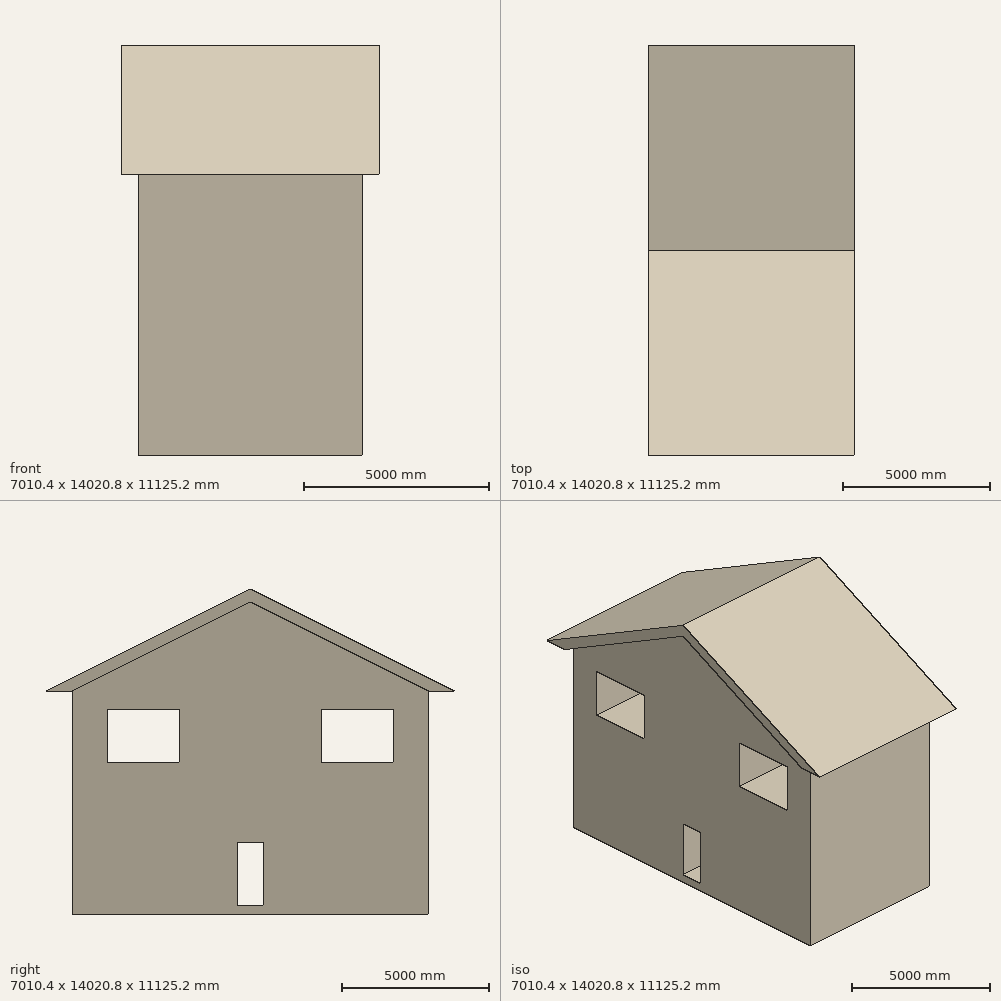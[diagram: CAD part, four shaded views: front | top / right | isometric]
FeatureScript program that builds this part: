
annotation { "Feature Type Name" : "Feature", "Feature Type Description" : "" }
export const myFeature = defineFeature(function(context is Context, id is Id, definition is map)
    precondition{}
    {
        {
            var Q0;
            Q0=qCreatedBy(makeId("Right.planeOp"),FACE);
            var sketch = newSketch(context, id + "F0", { "sketchPlane" : qUnion([Q0])});
            skLineSegment(sketch, "E0", {"start": v(0, 0) * mm, "end": v(-6096, 0) * mm});
            skLineSegment(sketch, "E1", {"start": v(-6096, 0) * mm, "end": v(-12192, 0) * mm});
            skLineSegment(sketch, "E2", {"start": v(-12192, 0) * mm, "end": v(-6096, 3048) * mm});
            skLineSegment(sketch, "E3", {"start": v(0, 0) * mm, "end": v(-6096, 3048) * mm});
            skLineSegment(sketch, "E4", {"start": v(-12192, 0) * mm, "end": v(-12192, -7315.2) * mm});
            skLineSegment(sketch, "E5", {"start": v(-12192, -7315.2) * mm, "end": v(0, -7315.2) * mm});
            skLineSegment(sketch, "E6", {"start": v(0, 0) * mm, "end": v(0, -7315.2) * mm});
            skLineSegment(sketch, "E7", {"start": v(-12192, -7315.2) * mm, "end": v(-12192, -7620) * mm});
            skLineSegment(sketch, "E8", {"start": v(0, -7315.2) * mm, "end": v(0, -7620) * mm});
            skLineSegment(sketch, "E9", {"start": v(-12192, -7620) * mm, "end": v(0, -7620) * mm});
            skLineSegment(sketch, "E10", {"start": v(-6096, -7315.2) * mm, "end": v(-6553.2, -7315.2) * mm});
            skLineSegment(sketch, "E11", {"start": v(-6553.2, -7315.2) * mm, "end": v(-6553.2, -5181.6) * mm});
            skLineSegment(sketch, "E12", {"start": v(-6553.2, -5181.6) * mm, "end": v(-5638.8, -5181.6) * mm});
            skLineSegment(sketch, "E13", {"start": v(-5638.8, -5181.6) * mm, "end": v(-5638.8, -7315.2) * mm});
            skLineSegment(sketch, "E14", {"start": v(-12192, 0) * mm, "end": v(-13106.4, 0) * mm});
            skLineSegment(sketch, "E15", {"start": v(0, 0) * mm, "end": v(914.4, 0) * mm});
            skLineSegment(sketch, "E16", {"start": v(-6096, 3048) * mm, "end": v(-6096, 3505.2) * mm});
            skLineSegment(sketch, "E17", {"start": v(-6096, 3505.2) * mm, "end": v(-13106.4, 0) * mm});
            skLineSegment(sketch, "E18", {"start": v(-6096, 3505.2) * mm, "end": v(914.4, 0) * mm});
            skLineSegment(sketch, "E19.bottom", {"start": v(-10668, -914.4) * mm, "end": v(-8839.2, -914.4) * mm});
            skLineSegment(sketch, "E19.top", {"start": v(-10668, -2133.6) * mm, "end": v(-8839.2, -2133.6) * mm});
            skLineSegment(sketch, "E19.left", {"start": v(-10668, -914.4) * mm, "end": v(-10668, -2133.6) * mm});
            skLineSegment(sketch, "E19.right", {"start": v(-8839.2, -914.4) * mm, "end": v(-8839.2, -2133.6) * mm});
            skLineSegment(sketch, "E20.bottom", {"start": v(-3352.8, -914.4) * mm, "end": v(-1524, -914.4) * mm});
            skLineSegment(sketch, "E20.top", {"start": v(-3352.8, -2133.6) * mm, "end": v(-1524, -2133.6) * mm});
            skLineSegment(sketch, "E20.left", {"start": v(-3352.8, -914.4) * mm, "end": v(-3352.8, -2133.6) * mm});
            skLineSegment(sketch, "E20.right", {"start": v(-1524, -914.4) * mm, "end": v(-1524, -2133.6) * mm});
            skLineSegment(sketch, "E21.0", {"start": v(-1219.2, -609.6) * mm, "end": v(-1219.2, -2438.4) * mm});
            skLineSegment(sketch, "E21.1", {"start": v(-3657.6, -609.6) * mm, "end": v(-1219.2, -609.6) * mm});
            skLineSegment(sketch, "E21.2", {"start": v(-3657.6, -609.6) * mm, "end": v(-3657.6, -2438.4) * mm});
            skLineSegment(sketch, "E21.3", {"start": v(-3657.6, -2438.4) * mm, "end": v(-1219.2, -2438.4) * mm});
            skLineSegment(sketch, "E22.0", {"start": v(-10972.8, -2438.4) * mm, "end": v(-8534.4, -2438.4) * mm});
            skLineSegment(sketch, "E22.1", {"start": v(-10972.8, -609.6) * mm, "end": v(-10972.8, -2438.4) * mm});
            skLineSegment(sketch, "E22.2", {"start": v(-10972.8, -609.6) * mm, "end": v(-8534.4, -609.6) * mm});
            skLineSegment(sketch, "E22.3", {"start": v(-8534.4, -609.6) * mm, "end": v(-8534.4, -2438.4) * mm});
            skSolve(sketch);
        }
        {
            var Q0;
            Q0=makeQuery(id+"F0.imprint","IMPRINT",FACE,{"disambiguationData":[TD([[makeQuery(id+"F0.imprint","IMPRINT",EDGE,{"derivedFrom":sQuery(id+"F0.wireOp",EDGE,"E2")}),1.0]])]});
            var Q1;
            Q1=makeQuery(id+"F0.imprint","IMPRINT",FACE,{"disambiguationData":[TD([[makeQuery(id+"F0.imprint","IMPRINT",EDGE,{"derivedFrom":sQuery(id+"F0.wireOp",EDGE,"E3")}),-1.0]])]});
            extrude(context, id + "F1", {"entities" : qUnion([Q0, Q1]), "endBound" : BoundingType.SYMMETRIC, "depth" : 7010.4 * mm, "offsetDistance" : 30.48 * mm});
        }
        {
            var Q0;
            Q0 = qSketchRegion(id + "F0", true);
            extrude(context, id + "F2", {"entities" : qUnion([Q0]), "operationType" : NewBodyOperationType.ADD, "endBound" : BoundingType.SYMMETRIC, "depth" : 6096 * mm, "offsetDistance" : 30.48 * mm});
        }
        {
            var Q0;
            Q0 = qSketchRegion(id + "F0", true);
            extrude(context, id + "F3", {"entities" : qUnion([Q0]), "operationType" : NewBodyOperationType.ADD, "depth" : 30.48 * mm, "offsetDistance" : 30.48 * mm});
        }
        {
            var Q0;
            Q0 = qSketchRegion(id + "F0", true);
            extrude(context, id + "F4", {"entities" : qUnion([Q0]), "operationType" : NewBodyOperationType.ADD, "depth" : 30.48 * mm, "offsetDistance" : 30.48 * mm});
        }
    });
